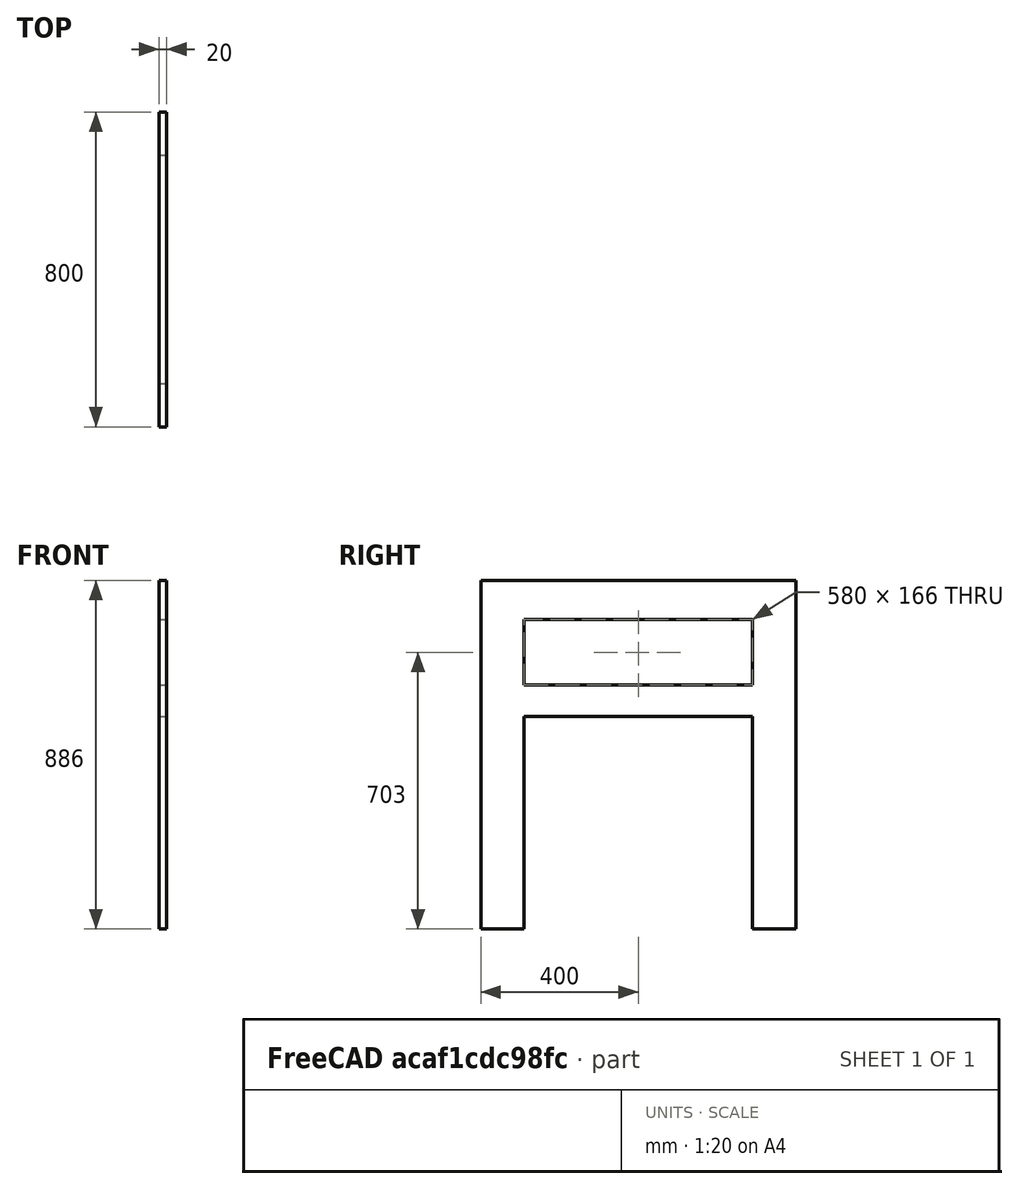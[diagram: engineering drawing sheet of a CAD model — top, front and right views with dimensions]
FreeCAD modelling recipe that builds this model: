
FCSTD DOCUMENT  (FreeCAD 0.20R29603 (Git))
Label: TrennwandKlein
License: All rights reserved
LicenseURL: http://en.wikipedia.org/wiki/All_rights_reserved
objects: Sketcher::SketchObject×1, PartDesign::Pad×1, PartDesign::Body×1
note: 4 computed .brp shape members not serialized (recipe doc carries the construction recipe); baked Part::Feature solids carry a one-line shape summary decoded from their .brp

FEATURE [Sketcher::SketchObject] Sketch
  FullyConstrained = true
  MapMode = 5
  Placement = pos=(0,0,0) rot=(0.57735,0.57735,0.57735;2.0944rad)
  Support = -> [YZ_Plane]
  sketch-geometry (12):
    g0: LineSegment StartX=-290 StartY=0 StartZ=0 EndX=-400 EndY=0 EndZ=0
    g1: LineSegment StartX=-400 StartY=0 StartZ=0 EndX=-400 EndY=886 EndZ=0
    g2: LineSegment StartX=-400 StartY=886 StartZ=0 EndX=400 EndY=886 EndZ=0
    g3: LineSegment StartX=400 StartY=886 StartZ=0 EndX=400 EndY=0 EndZ=0
    g4: LineSegment StartX=400 StartY=0 StartZ=0 EndX=290 EndY=0 EndZ=0
    g5: LineSegment StartX=290 StartY=0 StartZ=0 EndX=290 EndY=540 EndZ=0
    g6: LineSegment StartX=290 StartY=540 StartZ=0 EndX=-290 EndY=540 EndZ=0
    g7: LineSegment StartX=-290 StartY=540 StartZ=0 EndX=-290 EndY=0 EndZ=0
    g8: LineSegment StartX=-290 StartY=620 StartZ=0 EndX=290 EndY=620 EndZ=0
    g9: LineSegment StartX=290 StartY=620 StartZ=0 EndX=290 EndY=786 EndZ=0
    g10: LineSegment StartX=290 StartY=786 StartZ=0 EndX=-290 EndY=786 EndZ=0
    g11: LineSegment StartX=-290 StartY=786 StartZ=0 EndX=-290 EndY=620 EndZ=0
  constraints (33):
    c: PointOnObject(g0,g-1)
    c: PointOnObject(g0,g-1)
    c: Coincident(g0,g1)
    c: Vertical(g1)
    c: Coincident(g1,g2)
    c: Horizontal(g2)
    c: Coincident(g2,g3)
    c: Vertical(g3)
    c: Coincident(g3,g4)
    c: Coincident(g4,g5)
    c: Vertical(g5)
    c: Coincident(g5,g6)
    c: Horizontal(g6)
    c: Coincident(g6,g7)
    c: Coincident(g7,g0)
    c: Vertical(g7)
    c: Symmetric(g0,g4,g-2)
    c: Symmetric(g3,g0,g-2)
    c: Distance(g4) = 110
    c: Distance(g1) = 886
    c: Distance(g5,g2) = 346
    c: Distance(g2) = 800
    c: Coincident(g8,g9)
    c: Coincident(g9,g10)
    c: Coincident(g10,g11)
    c: Coincident(g11,g8)
    c: Horizontal(g10)
    c: Vertical(g9)
    c: Vertical(g11)
    c: Symmetric(g8,g8,g-2)
    c: Distance(g9,g3) = 110
    c: Distance(g9,g2) = 100
    c: Distance(g5,g8) = 80
FEATURE [PartDesign::Pad] Pad
  Direction = (1,-2e-16,3e-16)
  Length = 20
  Length2 = 10
  Placement = pos=(0,0,0) rot=(0.57735,0.57735,0.57735;2.0944rad)
  Profile = -> Sketch
  ReferenceAxis = -> Sketch [N_Axis]
  Type = 0
FEATURE [PartDesign::Body] Body
  Group = -> [Sketch,Pad]
  Origin = -> Origin
  Tip = -> Pad
